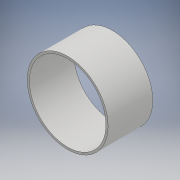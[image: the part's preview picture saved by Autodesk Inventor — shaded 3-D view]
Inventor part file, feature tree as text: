
AUTODESK INVENTOR PART (.ipt)
format: ipt  version: 2017 (Build 210142000, 142)  size: 100,864 bytes
history: native  units: mm
features: extrude x1, sketch x1
ambient origin geometry x8: Origin, YZ Plane, XZ Plane, XY Plane, X Axis, Y Axis, Z Axis, Center Point
bodies: Solid1 (feature_tree)
feature tree (2):
  extrude  "Extrusion1"  Depth=42.0mm
  sketch  "Sketch1"  dims[d0=76.0mm d1=2.0mm d2=42.0mm d3=0.0mm]
